# Revit family: DIVITYP002
name_source: partatom
category: Furniture
units: mm (PartAtom-declared; Revit-internal decimal feet)

## family parameters
Always vertical = Yes
Cut with Voids When Loaded = No
OmniClass Number = 23.40.20.00
OmniClass Title = General Furniture and Specialties
Render Appearance Source = Family Geometry
Room Calculation Point = No
Shared = No
Work Plane-Based = No

## types (1)
- DIVITYP002
    Cost = 46361 $
    Default Elevation = 0 mm  [stored 0 ft]
    Description = 3 x White Duplex Outlet - Line 1, 3 x White Duplex Outlet - Line 2, 3 x White Duplex Outlet - Line 3, 3 x White Duplex Outlet - Line 4 - Dedicated, 1 x 21 in. Electrical Jumper  (Extended Panel To Panel), 1 x RH Receptacle Mounted Base Infeed - 72L - 8 Wire, 4 Circuit, 3 x DiVi LINEAR BASE RACEWAY SHROUD 3-WAY 90 DEGREES, 1 x DiVi LINEAR BASE RACEWAY SHROUD 2-WAY 90 DEGREES, 4 x DiVi LINEAR HARD PANEL-PWR-PERM MONO- 42H X 72W, 7 x DiVi LINEAR Hard PANEL -NPWR-PERM MONO- 42H X 72W, 11 x DIVI LINEAR BASE RACEWAY SHROUD END OF RUN, 6 x Pedestal - Box,Box,File - 30D, 6 x Pedestal - F/F - 24D, 6 x Pedestal Extension Shroud, 6 x Silver Key Alike Kit (2 Cores) - Wesko Type, 6 x Rectangular - 2mm Edge - 24D x 42W, 6 x Rectangular - 2mm Edge - 30D x 72W, 18 x Flat Plate, 3 x Regular Cantilever - Left Hand - 30D, 3 x Regular Cantilever - Right Hand - 30D, 6 x U-Channel - 48W
    Exported From CET Designer = Yes
    Manufacturer = AIS
    Model = E-MW8W4DO1-W
    Show DIVITYP002 = Yes
    VisibilityIndex = 0

note: [stored X ft] marks values corroborated as IEEE doubles in the binary element streams (Revit-internal decimal feet)

## geometry (parser evidence)
native form markers: Sweep x3
no freeform markers — native parametric forms only
